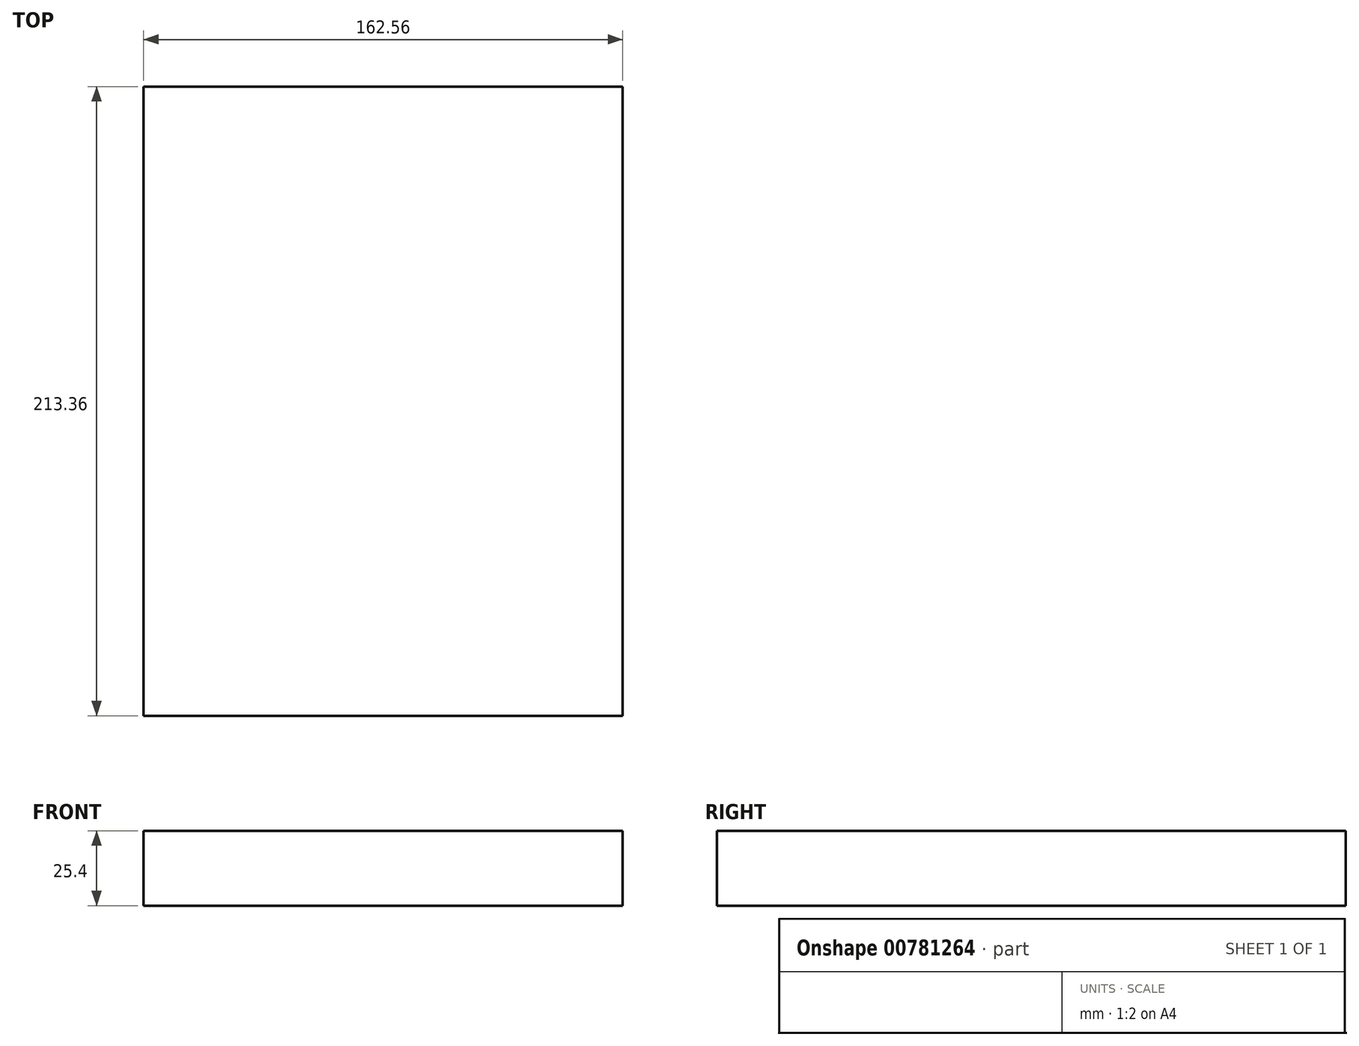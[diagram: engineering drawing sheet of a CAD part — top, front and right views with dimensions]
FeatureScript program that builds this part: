
annotation { "Feature Type Name" : "Feature", "Feature Type Description" : "" }
export const myFeature = defineFeature(function(context is Context, id is Id, definition is map)
    precondition{}
    {
        {
            var Q0;
            Q0=qCreatedBy(makeId("Top.planeOp"),FACE);
            var sketch = newSketch(context, id + "F0", { "sketchPlane" : qUnion([Q0])});
            skPoint(sketch, "E0.middle", {"position": v(0, 0) * mm});
            skLineSegment(sketch, "E1.0", {"start": v(-81.28, 106.68) * mm, "end": v(81.28, 106.68) * mm});
            skLineSegment(sketch, "E1.1", {"start": v(-81.28, 106.68) * mm, "end": v(-81.28, -106.68) * mm});
            skLineSegment(sketch, "E1.2", {"start": v(-81.28, -106.68) * mm, "end": v(81.28, -106.68) * mm});
            skLineSegment(sketch, "E1.3", {"start": v(81.28, 106.68) * mm, "end": v(81.28, -106.68) * mm});
            skSolve(sketch);
        }
        {
            var Q0;
            Q0=qSketchRegion(id+"F0",true);
            extrude(context, id + "F1", {"entities" : qUnion([Q0]), "depth" : 25.4 * mm, "offsetDistance" : 25.4 * mm});
        }
    });
